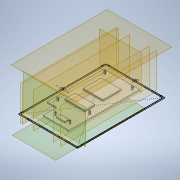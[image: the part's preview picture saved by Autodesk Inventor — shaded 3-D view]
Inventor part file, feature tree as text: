
AUTODESK INVENTOR PART (.ipt)
format: ipt  version: 2021 (Build 250183000, 183)  size: 373,760 bytes
history: native  units: in
note: dims shown in document units (in); Inventor stores cm internally (conversion verified against a paired STEP export)
features: sketch x23, extrude x16, reference x16, plane x9, other x4, revolve x2, mirror x1, chamfer x1
ambient origin geometry x8: Origin, YZ Plane, XZ Plane, XY Plane, X Axis, Y Axis, Z Axis, Center Point
bodies: Solid1 (feature_tree)
feature tree (72):
  sketch  "Sketch1"  dims[d0=3.937in d1=5.9055in]
  extrude  "Extrusion1"  Depth=5.9055in
  extrude  "Extrusion2"  Depth=0.0787in TaperAngle=0.0deg
  sketch  "Sketch2"  dims[d5=0.0787in d6=0.0in d7=-1.5748in]
  plane  "Work Plane1"
  extrude  "Extrusion3"  [1 undecoded]
  sketch  "Sketch7"  dims[d19=0.0787in d20=0.0in d21=2.8346in]
  plane  "Work Plane2"
  revolve  "Revolution2"  [1 undecoded]
  plane  "Work Plane3"
  extrude  "Extrusion4"  Depth=0.7087in
  sketch  "Sketch Driven Pattern1"  dims[d2=0.0787in d3=2.1654in d4=0.0in]
  extrude  "Extrusion5"  Depth=0.0787in
  plane  "Work Plane4"
  extrude  "Extrusion6"  Depth=0.7087in
  extrude  "Extrusion7"  Depth=0.1378in
  extrude  "Extrusion8"  Depth=0.1575in
  mirror  "Mirror1"
  plane  "Work Plane5"
  extrude  "Extrusion9"  Depth=3.0in
  extrude  "Extrusion10"  Depth=0.1946in
  extrude  "Extrusion11"  Depth=0.0787in TaperAngle=0.0deg
  chamfer  "Chamfer1"  Distance=0.0787in
  extrude  "Extrusion12"  Depth=1.1811in
  sketch  "Sketch22"  dims[d45=0.0906in d46=0.3819in]
  plane  "Work Plane6"
  revolve  "Revolution3"  [1 undecoded]
  extrude  "Extrusion13"  Depth=0.3819in
  sketch  "Sketch Driven Pattern2"  dims[d15=1.378in d16=1.2598in]
  sketch  "Sketch27"  dims[d52=0.5933in d53=0.0in d54=0.4724in]
  plane  "Work Plane7"
  extrude  "Extrusion14"  Depth=0.0866in
  plane  "Work Plane8"
  extrude  "Extrusion15"  Depth=0.3236in
  plane  "Work Plane9"
  extrude  "Extrusion16"  Depth=0.4724in
  sketch  "Sketch6"  dims[d17=1.0236in d18=0.7087in]
  reference  "Reference1"
  reference  "Reference2"
  reference  "Reference3"
  reference  "Reference4"
  sketch  "Sketch8"  dims[d22=0.7087in d23=0.1102in]
  sketch  "Sketch9"  dims[d26=0.1102in d27=0.1378in]
  sketch  "Sketch10"  dims[d28=0.1575in d29=0.0689in]
  reference  "Reference5"
  reference  "Reference6"
  reference  "Reference7"
  reference  "Reference8"
  reference  "Reference9"
  reference  "Reference10"
  sketch  "Sketch11"  dims[d30=90.0deg d31=3.0in]
  sketch  "Sketch13"  dims[d32=0.0394in d33=0.1946in]
  sketch  "Sketch15"  dims[d34=0.0299in d35=0.0787in d36=0.0in]
  sketch  "Sketch18"  dims[d37=0.0157in]
  sketch  "Sketch19"  dims[d38=0.0157in d39=0.0787in d40=0.0in]
  sketch  "Sketch20"  dims[d41=0.9055in d42=1.1811in]
  sketch  "Sketch21"  dims[d43=0.4606in d44=0.9843in]
  reference  "Reference11"
  reference  "Reference12"
  reference  "Reference13"
  reference  "Reference14"
  reference  "Reference15"
  reference  "Reference16"
  sketch  "Sketch25"  dims[d47=0.5933in d48=0.0in d49=0.0866in]
  sketch  "Sketch26"  dims[d50=0.4409in d51=0.3236in]
  sketch  "Sketch28"  dims[d55=0.5933in d56=0.0in]
  sketch  "Sketch29"  dims[d57=0.1575in d58=0.0787in d59=45.0deg]
  sketch  "Sketch30"  dims[d63=0.3937in d64=0.0906in d65=0.4606in d66=0.9843in d67=0.5933in d68=0.0in d69=0.0866in d70=0.4409in d71=0.3236in d72=0.5933in d73=0.0in d74=0.4724in d75=0.5933in d76=0.0in d77=0.2756in d78=0.5906in d79=0.0787in d80=0.0in d81=90.0deg d82=0.0276in d83=0.0394in d84=0.0in d85=-0.5in d86=4.5438in d87=0.0in d88=0.3125in d89=4.5438in d90=0.0in d91=1.125in d92=4.5438in d93=0.0in]
  other  "Chestbox_with_electronical_devices.iam"
  other  "ArduinoMega_STEP_AP203:1"
  other  "TCA9548A Adfruit with Header:1"
  other  "Part57"
note: 3 required parameter values undecoded (feature->parameter linkage not recoverable at this tier; creation-order binding heuristic only, values carry confidence <= 0.55)